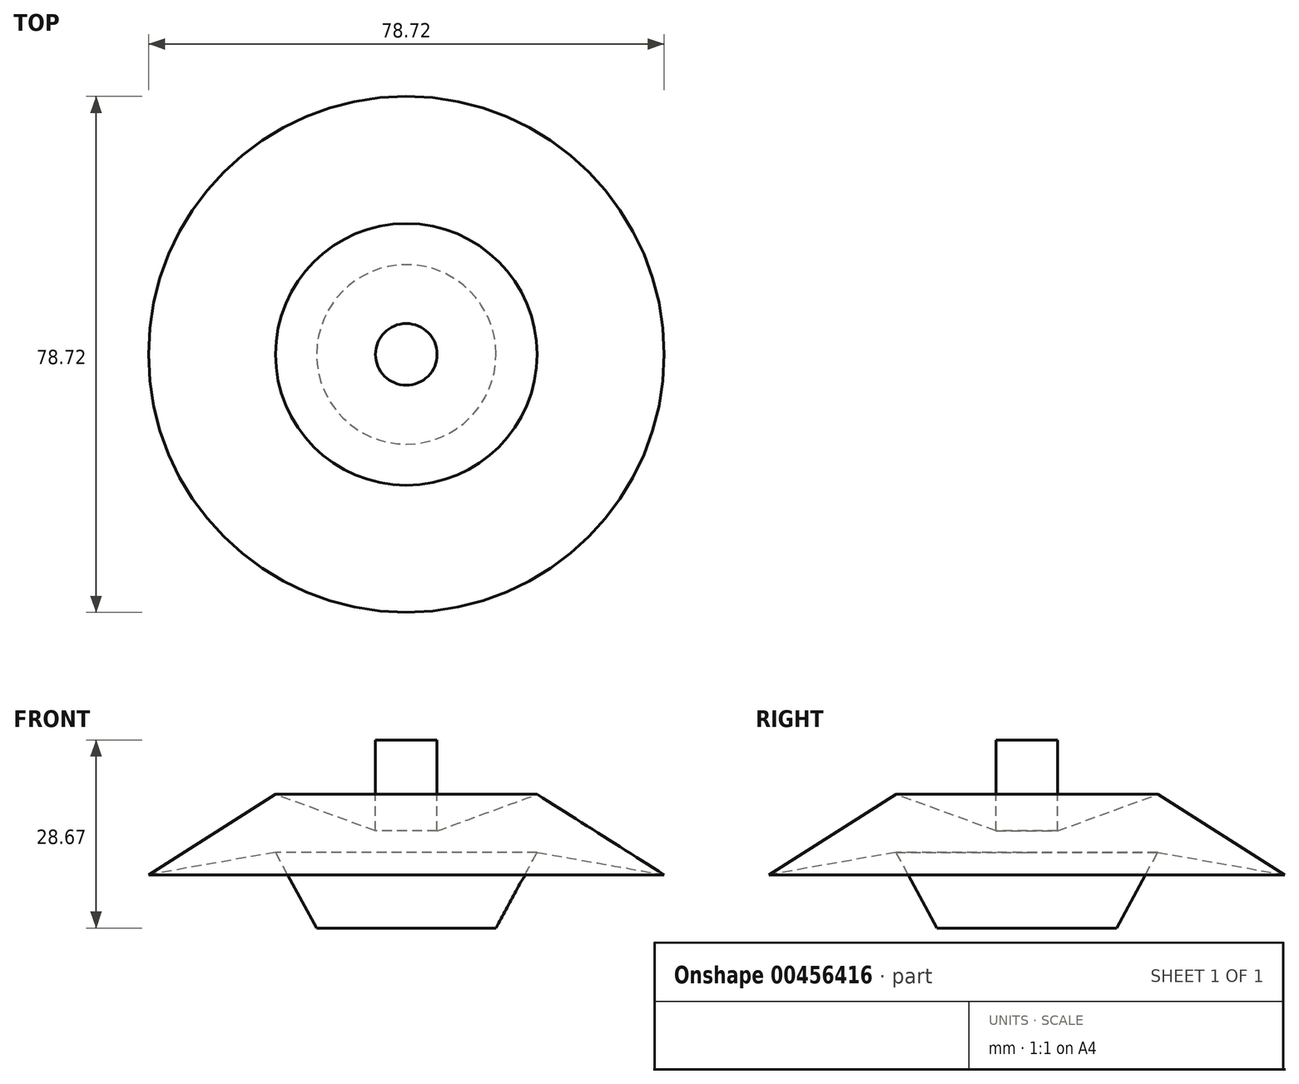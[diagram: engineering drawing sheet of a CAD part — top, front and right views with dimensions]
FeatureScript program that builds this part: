
annotation { "Feature Type Name" : "Feature", "Feature Type Description" : "" }
export const myFeature = defineFeature(function(context is Context, id is Id, definition is map)
    precondition{}
    {
        {
            var Q0;
            Q0=qCreatedBy(makeId("Front.planeOp"),FACE);
            var sketch = newSketch(context, id + "F0", { "sketchPlane" : qUnion([Q0])});
            skLineSegment(sketch, "E0", {"start": v(0, 0) * mm, "end": v(13.7, 0) * mm});
            skLineSegment(sketch, "E1", {"start": v(13.7, 0) * mm, "end": v(19.97, 11.55) * mm});
            skLineSegment(sketch, "E2", {"start": v(19.97, 11.55) * mm, "end": v(39.36, 8.13) * mm});
            skLineSegment(sketch, "E3", {"start": v(39.36, 8.13) * mm, "end": v(19.97, 20.4) * mm});
            skLineSegment(sketch, "E4", {"start": v(19.97, 20.4) * mm, "end": v(8.27, 16.12) * mm});
            skLineSegment(sketch, "E5", {"start": v(8.27, 16.12) * mm, "end": v(4.7, 14.8) * mm});
            skLineSegment(sketch, "E6", {"start": v(4.7, 14.8) * mm, "end": v(4.7, 42.64) * mm});
            skLineSegment(sketch, "E7", {"start": v(4.7, 42.64) * mm, "end": v(0, 42.64) * mm});
            skLineSegment(sketch, "E8", {"start": v(0, 42.64) * mm, "end": v(0, 0) * mm});
            skSolve(sketch);
        }
        {
            var Q0;
            Q0=makeQuery(id+"F0.imprint","IMPRINT",FACE,{"disambiguationData":[TD([[makeQuery(id+"F0.imprint","IMPRINT",EDGE,{"derivedFrom":sQuery(id+"F0.wireOp",EDGE,"E0")}),1.0]])]});
            var Q1;
            Q1=sQuery(id+"F0.wireOp",EDGE,"E8");
            revolve(context, id + "F1", {"entities" : qUnion([Q0]), "axis" : qUnion([Q1]), "revolveType" : RevolveType.FULL});
        }
        {
            var Q0;
            Q0=makeQuery(id+"F1.opRevolve","SWEPT_FACE",FACE,{"disambiguationData":[OSD([sQuery(id+"F0.wireOp",EDGE,"E7")])]});
            extrude(context, id + "F2", {"entities" : qUnion([Q0]), "operationType" : NewBodyOperationType.REMOVE, "oppositeDirection" : true, "depth" : 13.97 * mm});
        }
    });
